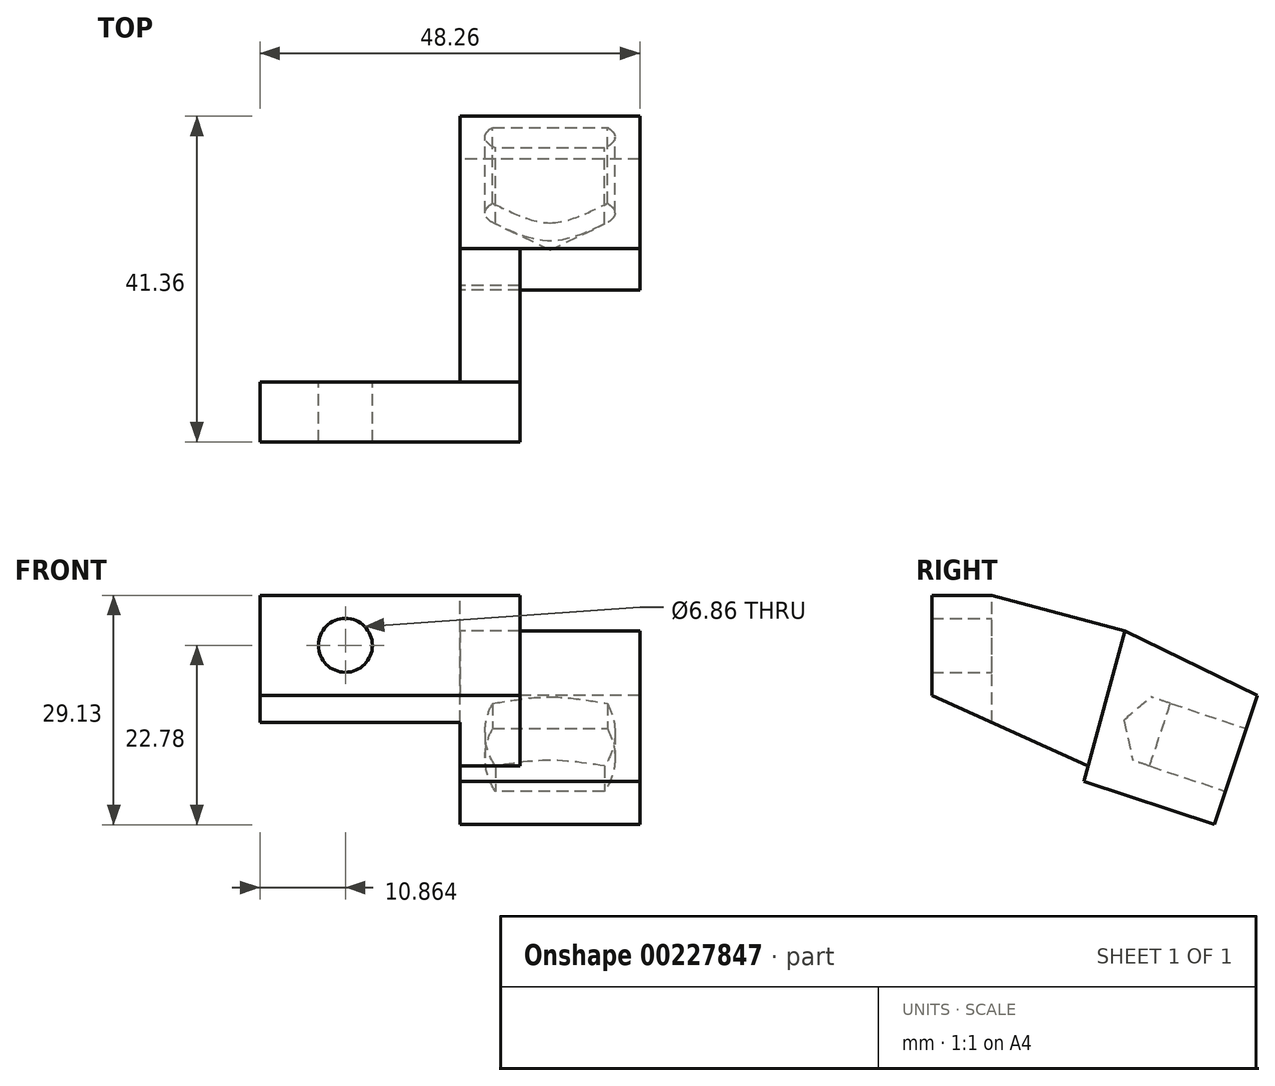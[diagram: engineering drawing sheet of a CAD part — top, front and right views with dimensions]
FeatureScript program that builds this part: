
annotation { "Feature Type Name" : "Feature", "Feature Type Description" : "" }
export const myFeature = defineFeature(function(context is Context, id is Id, definition is map)
    precondition{}
    {
        {
            var Q0;
            Q0=qCreatedBy(makeId("Front.planeOp"),FACE);
            var sketch = newSketch(context, id + "F0", { "sketchPlane" : qUnion([Q0])});
            skLineSegment(sketch, "E0.bottom", {"start": v(0, 0) * mm, "end": v(-25.4, 0) * mm});
            skLineSegment(sketch, "E0.top", {"start": v(0, 12.7) * mm, "end": v(-25.4, 12.7) * mm});
            skLineSegment(sketch, "E0.left", {"start": v(0, 0) * mm, "end": v(0, 12.7) * mm});
            skLineSegment(sketch, "E0.right", {"start": v(-25.4, 0) * mm, "end": v(-25.4, 12.7) * mm});
            skPoint(sketch, "E1", {"position": v(-14.54, 6.35) * mm});
            skSolve(sketch);
        }
        {
            var Q0;
            Q0=makeQuery(id+"F0.imprint","IMPRINT",FACE,{"disambiguationData":[TD([[makeQuery(id+"F0.imprint","IMPRINT",EDGE,{"derivedFrom":sQuery(id+"F0.wireOp",EDGE,"E0.bottom")}),-1.0]])]});
            extrude(context, id + "F1", {"entities" : qUnion([Q0]), "endBound" : BoundingType.SYMMETRIC, "depth" : 7.62 * mm});
        }
        {
            var Q0;
            Q0=qCreatedBy(makeId("Right.planeOp"),FACE);
            var sketch = newSketch(context, id + "F2", { "sketchPlane" : qUnion([Q0])});
            skLineSegment(sketch, "E2", {"start": v(16.04, -8.96) * mm, "end": v(-3.8, 0) * mm});
            skLineSegment(sketch, "E3", {"start": v(-3.8, 0) * mm, "end": v(-3.8, 12.7) * mm});
            skLineSegment(sketch, "E4", {"start": v(3.8, 12.7) * mm, "end": v(-3.8, 12.7) * mm});
            skLineSegment(sketch, "E5", {"start": v(16.04, -8.96) * mm, "end": v(20.74, 8.18) * mm});
            skLineSegment(sketch, "E6", {"start": v(20.74, 8.18) * mm, "end": v(3.8, 12.7) * mm});
            skSolve(sketch);
        }
        {
            var Q0;
            Q0=qSketchRegion(id+"F2",true);
            var Q1;
            Q1=makeQuery(id+"F1.opExtrude","SWEPT_FACE",FACE,{"disambiguationData":[OSD([sQuery(id+"F0.wireOp",EDGE,"E0.left")])]});
            extrude(context, id + "F3", {"entities" : qUnion([Q0]), "operationType" : NewBodyOperationType.ADD, "endBoundEntityFace" : qUnion([Q1]), "depth" : 7.62 * mm});
        }
        {
            var Q0;
            Q0=qCreatedBy(makeId("Right.planeOp"),FACE);
            var sketch = newSketch(context, id + "F4", { "sketchPlane" : qUnion([Q0])});
            skLineSegment(sketch, "E7", {"start": v(37.55, 0) * mm, "end": v(32.09, -16.43) * mm});
            skLineSegment(sketch, "E8", {"start": v(16.04, -8.95) * mm, "end": v(20.72, 8.2) * mm});
            skLineSegment(sketch, "E9", {"start": v(20.72, 8.2) * mm, "end": v(37.55, 0) * mm});
            skLineSegment(sketch, "E10", {"start": v(32.09, -16.43) * mm, "end": v(16.04, -8.95) * mm});
            skSolve(sketch);
        }
        {
            var Q0;
            Q0=makeQuery(id+"F4.imprint","IMPRINT",FACE,{"disambiguationData":[TD([[makeQuery(id+"F4.imprint","IMPRINT",EDGE,{"derivedFrom":sQuery(id+"F4.wireOp",EDGE,"E7")}),-1.0]])]});
            extrude(context, id + "F5", {"entities" : qUnion([Q0]), "operationType" : NewBodyOperationType.ADD, "depth" : 22.86 * mm});
        }
        {
            var Q0;
            Q0=makeQuery(id+"F5.opExtrude","SWEPT_FACE",FACE,{"disambiguationData":[OSD([sQuery(id+"F4.wireOp",EDGE,"E7")])]});
            var sketch = newSketch(context, id + "F6", { "sketchPlane" : qUnion([Q0])});
            skPoint(sketch, "E11", {"position": v(-11.45, 3.48) * mm});
            skLineSegment(sketch, "E12.bottom", {"start": v(0, 11.84) * mm, "end": v(-22.86, 11.84) * mm});
            skLineSegment(sketch, "E12.top", {"start": v(0, 7.38) * mm, "end": v(-22.86, 7.38) * mm});
            skLineSegment(sketch, "E12.left", {"start": v(0, 11.84) * mm, "end": v(0, 7.38) * mm});
            skLineSegment(sketch, "E12.right", {"start": v(-22.86, 11.84) * mm, "end": v(-22.86, 7.38) * mm});
            skLineSegment(sketch, "E13.bottom", {"start": v(-22.86, 11.84) * mm, "end": v(0, 11.84) * mm});
            skLineSegment(sketch, "E13.top", {"start": v(-22.86, -1) * mm, "end": v(0, -1) * mm});
            skLineSegment(sketch, "E13.left", {"start": v(-22.86, -1) * mm, "end": v(-22.86, 11.84) * mm});
            skLineSegment(sketch, "E13.right", {"start": v(0, -1) * mm, "end": v(0, 11.84) * mm});
            skSolve(sketch);
        }
        {
            var Q0;
            Q0=sQuery(id+"F6.wireOp",VERTEX,"E11");
            var Q1;
            Q1=makeQuery(id+"F1.opExtrude","SWEPT_BODY",BODY,{"disambiguationData":[OSD([sQuery(id+"F0.wireOp",EDGE,"E0.bottom"),sQuery(id+"F0.wireOp",EDGE,"E0.top"),sQuery(id+"F0.wireOp",EDGE,"E0.left"),sQuery(id+"F0.wireOp",EDGE,"E0.right")])]});
            hole(context, id + "F7", {"style" : HoleStyle.SIMPLE, "endStyle" : HoleEndStyle.BLIND, "holeDiameter" : 16.5 * mm, "holeDepth" : 10.16 * mm, "locations" : qUnion([Q0]), "scope" : qUnion([Q1]), "tappedDepth" : 12.7 * mm, "tapClearance" : 3});
        }
        {
            var Q0;
            Q0=sQuery(id+"F0.wireOp",VERTEX,"E1");
            var Q1;
            Q1=makeQuery(id+"F1.opExtrude","SWEPT_BODY",BODY,{"disambiguationData":[OSD([sQuery(id+"F0.wireOp",EDGE,"E0.bottom"),sQuery(id+"F0.wireOp",EDGE,"E0.top"),sQuery(id+"F0.wireOp",EDGE,"E0.left"),sQuery(id+"F0.wireOp",EDGE,"E0.right")])]});
            hole(context, id + "F8", {"style" : HoleStyle.SIMPLE, "endStyle" : HoleEndStyle.BLIND, "oppositeDirection" : true, "holeDiameter" : 6.86 * mm, "holeDepth" : 76.2 * mm, "locations" : qUnion([Q0]), "scope" : qUnion([Q1])});
        }
        {
            var Q0;
            {var subQ1=sQuery(id+"F2.wireOp",EDGE,"kXSC0KOg-fQ94-LhOI-q1H8-9R4feyNPQgDR");var subQ2=sQuery(id+"F0.wireOp",EDGE,"E0.bottom");var subQ3=sQuery(id+"F2.wireOp",EDGE,"L1goWyKu-SLoI-iGnL-KQ5P-oYqGf497itw2");var subQ4=sQuery(id+"F2.wireOp",EDGE,"E2");var subQ5=sQuery(id+"F2.wireOp",EDGE,"E3");Q0=makeQuery(id+"F5.boolean.opBoolean","MERGE",FACE,{"derivedFrom":[makeQuery(id+"F3.boolean.opBoolean","SPLIT",FACE,{"disambiguationData":[TD([makeQuery(id+"F1.opExtrude","SWEPT_FACE",FACE,{"disambiguationData":[OSD([subQ2])]})])],"derivedFrom":makeQuery(id+"F3.opExtrude","CAP_FACE",FACE,{"disambiguationData":[OSD([subQ1,subQ4,subQ5,sQuery(id+"F2.wireOp",EDGE,"LLgOkjW7-WFPW-9obn-Mb4V-AVdvvsvQ1woF"),subQ3])],"isStart":true})}),makeQuery(id+"F5.opExtrude","CAP_FACE",FACE,{"disambiguationData":[OSD([sQuery(id+"F4.wireOp",EDGE,"E7"),sQuery(id+"F4.wireOp",EDGE,"lPFBrdxe-zxQl-zXDA-f7J2-miDMy3g2819J"),sQuery(id+"F4.wireOp",EDGE,"E8"),sQuery(id+"F4.wireOp",EDGE,"E9")])],"isStart":true})]});}
            var sketch = newSketch(context, id + "F9", { "sketchPlane" : qUnion([Q0])});
            skLineSegment(sketch, "E14", {"start": v(-3.81, 0) * mm, "end": v(-3.81, -3.44) * mm});
            skLineSegment(sketch, "E15", {"start": v(-3.81, -3.44) * mm, "end": v(3.8, 0) * mm});
            skLineSegment(sketch, "E16", {"start": v(3.8, 0) * mm, "end": v(-3.81, 0) * mm});
            skSolve(sketch);
        }
        {
            var Q0;
            Q0=makeQuery(id+"F9.imprint","IMPRINT",FACE,{"disambiguationData":[TD([[makeQuery(id+"F9.imprint","IMPRINT",EDGE,{"derivedFrom":sQuery(id+"F9.wireOp",EDGE,"E14")}),1.0]])]});
            var Q1;
            Q1=makeQuery(id+"F1.opExtrude","SWEPT_FACE",FACE,{"disambiguationData":[OSD([sQuery(id+"F0.wireOp",EDGE,"E0.right")])]});
            extrude(context, id + "F10", {"entities" : qUnion([Q0]), "operationType" : NewBodyOperationType.ADD, "endBound" : BoundingType.UP_TO_SURFACE, "endBoundEntityFace" : qUnion([Q1]), "depth" : 21.59 * mm});
        }
        {
            var Q0;
            {var subQ0=sQuery(id+"F6.wireOp",EDGE,"E13.top");Q0=makeQuery(id+"F6.imprint","IMPRINT",FACE,{"disambiguationData":[TD([[makeQuery(id+"F6.imprint","IMPRINT",EDGE,{"derivedFrom":subQ0}),-1.0]])]});}
            var Q1;
            {var subQ0=sQuery(id+"F6.wireOp",EDGE,"E12.top");Q1=makeQuery(id+"F6.imprint","IMPRINT",FACE,{"disambiguationData":[TD([[makeQuery(id+"F6.imprint","IMPRINT",EDGE,{"derivedFrom":subQ0}),-1.0]])]});}
            var Q2;
            Q2=makeQuery(id+"F5.opExtrude","SWEPT_FACE",FACE,{"disambiguationData":[OSD([sQuery(id+"F4.wireOp",EDGE,"E9")])]});
            var Q3;
            Q3=makeQuery(id+"F5.opExtrude","SWEPT_FACE",FACE,{"disambiguationData":[OSD([sQuery(id+"F4.wireOp",EDGE,"E8")])]});
            extrude(context, id + "F11", {"entities" : qUnion([Q0, Q1, Q2]), "operationType" : NewBodyOperationType.ADD, "endBound" : BoundingType.UP_TO_SURFACE, "oppositeDirection" : true, "endBoundEntityFace" : qUnion([Q3]), "depth" : 22.9 * mm});
        }
        {
            var Q0;
            Q0=sQuery(id+"F0.wireOp",VERTEX,"E1");
            var Q1;
            Q1=makeQuery(id+"F1.opExtrude","SWEPT_BODY",BODY,{"disambiguationData":[OSD([sQuery(id+"F0.wireOp",EDGE,"E0.bottom"),sQuery(id+"F0.wireOp",EDGE,"E0.top"),sQuery(id+"F0.wireOp",EDGE,"E0.left"),sQuery(id+"F0.wireOp",EDGE,"E0.right")])]});
            hole(context, id + "F12", {"style" : HoleStyle.SIMPLE, "endStyle" : HoleEndStyle.BLIND, "holeDiameter" : 6.86 * mm, "holeDepth" : 76.2 * mm, "locations" : qUnion([Q0]), "scope" : qUnion([Q1])});
        }
    });
